# Revit family: Spannklauen Montagesatz Stahl 35+36
name_source: partatom
category: HLS-Bauteile
revit_build: Autodesk Revit 2017 (Build: 20190507_1515(x64)
units: mm (PartAtom-declared; Revit-internal decimal feet)

## family parameters
Arbeitsebenenbasiert = Nein
Beim Laden mit Abzugskörper schneiden = Nein
Bemaßung runder Anschluss = Durchmesser verwenden
Gemeinsam genutzt = Ja
Immer vertikal = Nein
Raumberechnungspunkt = Nein
Teiletyp = Normal

## types (1)
- Spannklauen Montagesatz Stahl 35+36
    Artikelnummer = 0814595
    Breite = 0 mm  [stored 0 ft]
    EAN = 4250928420077
    Fabrikat = MEFA
    Firma = MEFA Befestigungs- und Montagesysteme GmbH
    Gewicht = 0.55 kg
    Gewicht pro Bauteil = 0.55 kg
    Gewindestifttyp = M10 x 110
    H = 42 mm  [stored 0.137795 ft]
    Höhe Profil = 42 mm  [stored 0.137795 ft]
    Klemmdicke = 26 mm
    Kurztext1 = Spannklaue Set C-Profil 35
    Kurztext2 = Profilhöhe bis 42 mm Klemmdicke 26 mm
    Länge = 0 mm  [stored 0 ft]
    Material = Stahl
    Oberflaeche = galvanisch verzinkt
    Profil = C-Profil
    Profiltyp = 35
    Stärke = 0 mm  [stored 0 ft]
    max. zul. Last = 0.00 kN

note: [stored X ft] marks values corroborated as IEEE doubles in the binary element streams (Revit-internal decimal feet)

## geometry (parser evidence)
native form markers: Sweep x1
no freeform markers — native parametric forms only
